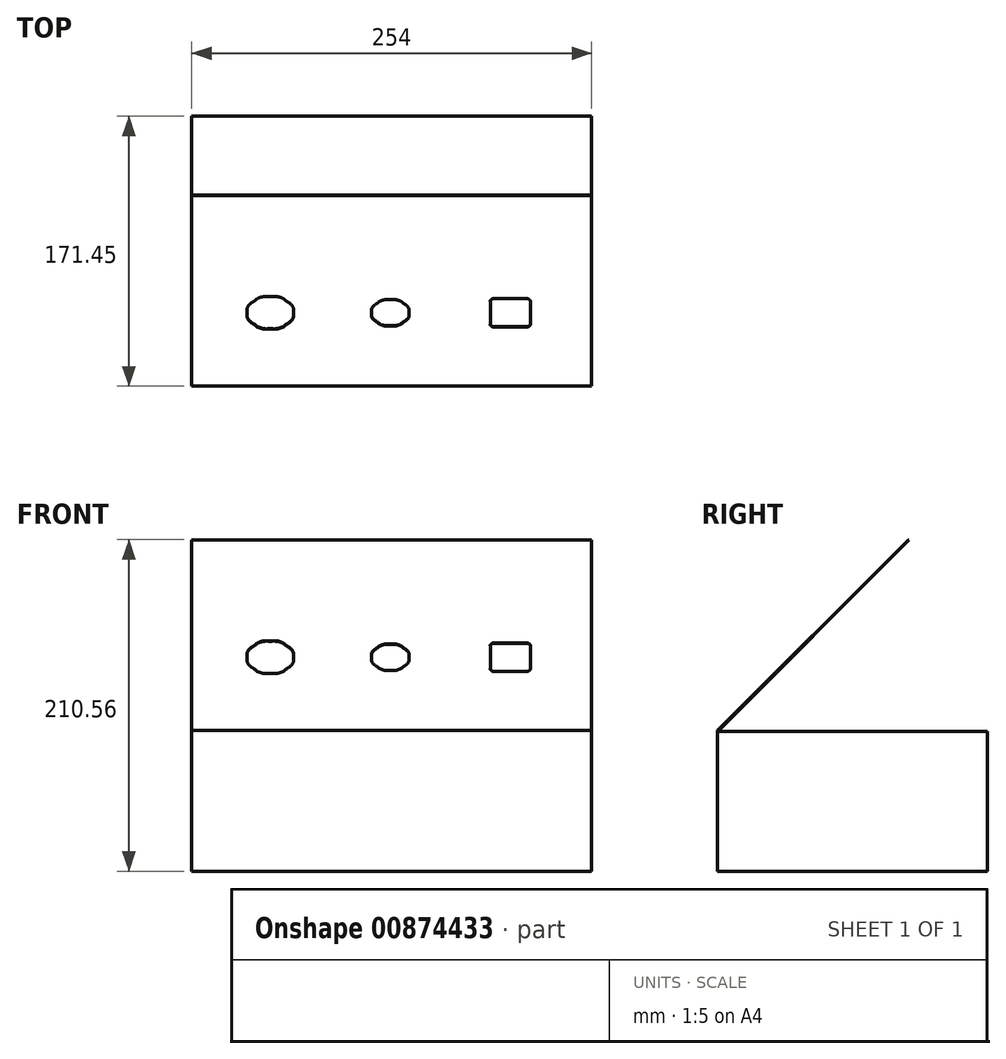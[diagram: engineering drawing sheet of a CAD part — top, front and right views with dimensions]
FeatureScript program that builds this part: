
annotation { "Feature Type Name" : "Feature", "Feature Type Description" : "" }
export const myFeature = defineFeature(function(context is Context, id is Id, definition is map)
    precondition{}
    {
        {
            var Q0;
            Q0=qCreatedBy(makeId("Right.planeOp"),FACE);
            var sketch = newSketch(context, id + "F0", { "sketchPlane" : qUnion([Q0])});
            skLineSegment(sketch, "E0.bottom", {"start": v(0, 0) * mm, "end": v(-171.45, 0) * mm});
            skLineSegment(sketch, "E0.top", {"start": v(0, 88.9) * mm, "end": v(-171.04, 88.9) * mm});
            skLineSegment(sketch, "E0.left", {"start": v(0, 0) * mm, "end": v(0, 88.9) * mm});
            skLineSegment(sketch, "E0.right", {"start": v(-171.45, 0) * mm, "end": v(-171.45, 89.32) * mm});
            skLineSegment(sketch, "E1", {"start": v(-171.45, 89.32) * mm, "end": v(-50.22, 210.56) * mm});
            skLineSegment(sketch, "E2", {"start": v(-50.22, 210.56) * mm, "end": v(-49.93, 210.27) * mm});
            skLineSegment(sketch, "E3", {"start": v(-49.93, 210.27) * mm, "end": v(-171.04, 89.15) * mm});
            skLineSegment(sketch, "E4", {"start": v(-171.04, 88.9) * mm, "end": v(-171.04, 89.15) * mm});
            skLineSegment(sketch, "E5", {"start": v(-171.04, 88.9) * mm, "end": v(-171.45, 88.9) * mm, "construction": true});
            skSolve(sketch);
        }
        {
            var Q0;
            Q0=qSketchRegion(id+"F0",true);
            extrude(context, id + "F1", {"entities" : qUnion([Q0]), "endBound" : BoundingType.SYMMETRIC, "depth" : 254 * mm, "offsetDistance" : 25.4 * mm});
        }
        {
            var Q0;
            Q0=makeQuery(id+"F1.opExtrude","SWEPT_FACE",FACE,{"disambiguationData":[OSD([sQuery(id+"F0.wireOp",EDGE,"E1")])]});
            var sketch = newSketch(context, id + "F2", { "sketchPlane" : qUnion([Q0])});
            skLineSegment(sketch, "E6", {"start": v(-127.94, 113.83) * mm, "end": v(126.06, 113.83) * mm, "construction": true});
            skLineSegment(sketch, "E7", {"start": v(-127.94, -55.63) * mm, "end": v(-127.94, 113.83) * mm, "construction": true});
            skLineSegment(sketch, "E8", {"start": v(126.06, -55.63) * mm, "end": v(126.06, 113.83) * mm, "construction": true});
            skLineSegment(sketch, "E9", {"start": v(87.96, -2.45) * mm, "end": v(87.96, 18.18) * mm});
            skLineSegment(sketch, "E10", {"start": v(85.58, 20.57) * mm, "end": v(64.94, 20.57) * mm});
            skLineSegment(sketch, "E11", {"start": v(64.94, -4.83) * mm, "end": v(85.58, -4.83) * mm});
            skLineSegment(sketch, "E12", {"start": v(62.56, 18.18) * mm, "end": v(62.56, -2.45) * mm});
            skLineSegment(sketch, "E13", {"start": v(126.06, -55.63) * mm, "end": v(-127.94, -55.63) * mm, "construction": true});
            skFitSpline(sketch, "E14", {"points": [v(-77.14, 22.55) * mm, v(-80.98, 22.55) * mm, v(-84.8, 20.97) * mm, v(-87.52, 18.25) * mm]});
            skFitSpline(sketch, "E15", {"points": [v(-87.52, 18.25) * mm, v(-90.24, 15.53) * mm, v(-91.82, 11.7) * mm, v(-91.82, 7.87) * mm, v(-91.82, 4.02) * mm, v(-90.24, 0.2) * mm, v(-87.52, -2.52) * mm]});
            skFitSpline(sketch, "E16", {"points": [v(-87.52, -2.52) * mm, v(-84.8, -5.24) * mm, v(-80.98, -6.82) * mm, v(-77.14, -6.82) * mm, v(-73.3, -6.82) * mm, v(-69.47, -5.24) * mm, v(-66.76, -2.52) * mm]});
            skFitSpline(sketch, "E17", {"points": [v(-66.76, -2.52) * mm, v(-64.04, 0.2) * mm, v(-62.46, 4.02) * mm, v(-62.46, 7.87) * mm, v(-62.46, 11.7) * mm, v(-64.04, 15.53) * mm, v(-66.76, 18.25) * mm]});
            skFitSpline(sketch, "E18", {"points": [v(-66.76, 18.25) * mm, v(-69.47, 20.97) * mm, v(-73.3, 22.55) * mm, v(-77.14, 22.55) * mm]});
            skFitSpline(sketch, "E19", {"points": [v(-0.94, 19.77) * mm, v(-4.06, 19.77) * mm, v(-7.15, 18.49) * mm, v(-9.36, 16.28) * mm]});
            skFitSpline(sketch, "E20", {"points": [v(-9.36, 16.28) * mm, v(-11.56, 14.08) * mm, v(-12.85, 10.98) * mm, v(-12.85, 7.87) * mm, v(-12.85, 4.75) * mm, v(-11.56, 1.65) * mm, v(-9.36, -0.55) * mm]});
            skFitSpline(sketch, "E21", {"points": [v(-9.36, -0.55) * mm, v(-7.15, -2.76) * mm, v(-4.06, -4.04) * mm, v(-0.94, -4.04) * mm, v(2.18, -4.04) * mm, v(5.27, -2.76) * mm, v(7.48, -0.55) * mm]});
            skFitSpline(sketch, "E22", {"points": [v(7.48, -0.55) * mm, v(9.68, 1.65) * mm, v(10.97, 4.75) * mm, v(10.97, 7.87) * mm, v(10.97, 10.98) * mm, v(9.68, 14.08) * mm, v(7.48, 16.28) * mm]});
            skFitSpline(sketch, "E23", {"points": [v(7.48, 16.28) * mm, v(5.27, 18.49) * mm, v(2.18, 19.77) * mm, v(-0.94, 19.77) * mm]});
            skFitSpline(sketch, "E24", {"points": [v(87.96, 18.18) * mm, v(87.96, 18.8) * mm, v(87.7, 19.43) * mm, v(87.26, 19.87) * mm]});
            skFitSpline(sketch, "E25", {"points": [v(87.26, 19.87) * mm, v(86.82, 20.3) * mm, v(86.2, 20.57) * mm, v(85.58, 20.57) * mm]});
            skFitSpline(sketch, "E26", {"points": [v(85.58, -4.83) * mm, v(86.2, -4.83) * mm, v(86.82, -4.58) * mm, v(87.26, -4.14) * mm]});
            skFitSpline(sketch, "E27", {"points": [v(87.26, -4.14) * mm, v(87.7, -3.7) * mm, v(87.96, -3.08) * mm, v(87.96, -2.45) * mm]});
            skFitSpline(sketch, "E28", {"points": [v(62.56, -2.45) * mm, v(62.56, -3.08) * mm, v(62.82, -3.7) * mm, v(63.26, -4.14) * mm]});
            skFitSpline(sketch, "E29", {"points": [v(63.26, -4.14) * mm, v(63.7, -4.58) * mm, v(64.32, -4.83) * mm, v(64.94, -4.83) * mm]});
            skFitSpline(sketch, "E30", {"points": [v(64.94, 20.57) * mm, v(64.32, 20.57) * mm, v(63.7, 20.3) * mm, v(63.26, 19.87) * mm]});
            skFitSpline(sketch, "E31", {"points": [v(63.26, 19.87) * mm, v(62.82, 19.43) * mm, v(62.56, 18.8) * mm, v(62.56, 18.18) * mm]});
            skSolve(sketch);
        }
        {
            var Q0;
            Q0=qSketchRegion(id+"F2",true);
            var Q1;
            Q1=makeQuery(id+"F1.opExtrude","SWEPT_FACE",FACE,{"disambiguationData":[OSD([sQuery(id+"F0.wireOp",EDGE,"E3")])]});
            extrude(context, id + "F3", {"entities" : qUnion([Q0]), "operationType" : NewBodyOperationType.REMOVE, "endBound" : BoundingType.UP_TO_SURFACE, "oppositeDirection" : true, "depth" : 25.4 * mm, "endBoundEntityFace" : qUnion([Q1]), "offsetDistance" : 25.4 * mm});
        }
    });
